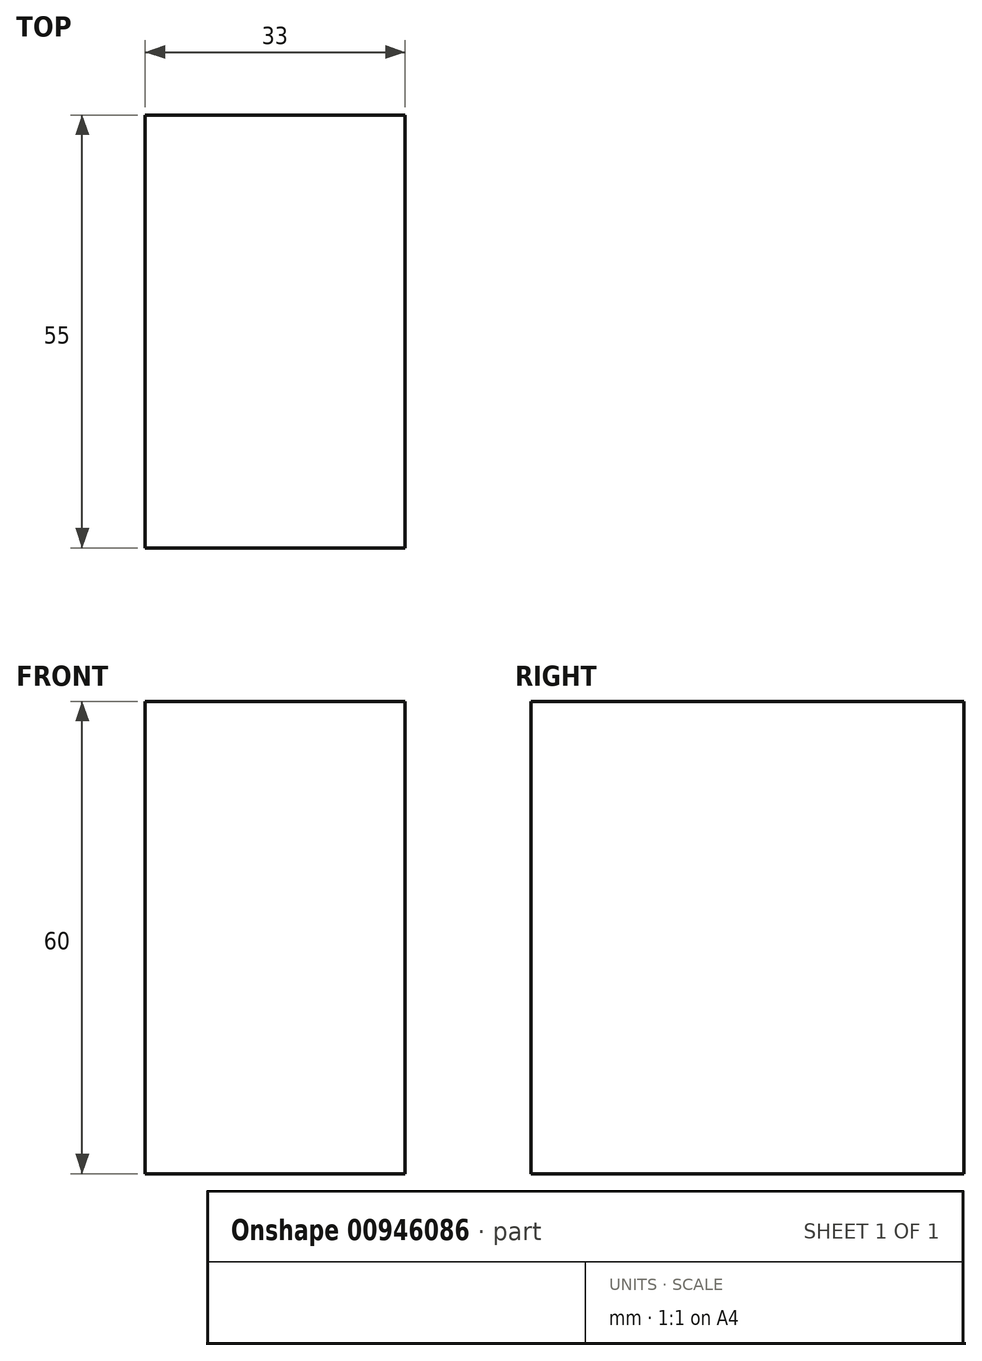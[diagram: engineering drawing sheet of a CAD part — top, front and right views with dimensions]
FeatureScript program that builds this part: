
annotation { "Feature Type Name" : "Feature", "Feature Type Description" : "" }
export const myFeature = defineFeature(function(context is Context, id is Id, definition is map)
    precondition{}
    {
        {
            var Q0;
            Q0=qCreatedBy(makeId("Top.planeOp"),FACE);
            var sketch = newSketch(context, id + "F0", { "sketchPlane" : qUnion([Q0])});
            skLineSegment(sketch, "E0.bottom", {"start": v(-49.38, 33.56) * mm, "end": v(-16.38, 33.56) * mm});
            skLineSegment(sketch, "E0.top", {"start": v(-49.38, -21.44) * mm, "end": v(-16.38, -21.44) * mm});
            skLineSegment(sketch, "E0.left", {"start": v(-49.38, 33.56) * mm, "end": v(-49.38, -21.44) * mm});
            skLineSegment(sketch, "E0.right", {"start": v(-16.38, 33.56) * mm, "end": v(-16.38, -21.44) * mm});
            skSolve(sketch);
        }
        {
            var Q0;
            Q0=qSketchRegion(id+"F0",true);
            extrude(context, id + "F1", {"entities" : qUnion([Q0]), "depth" : 60 * mm, "offsetDistance" : 25 * mm});
        }
    });
